# Revit family: BMP250710
name_source: partatom
category: Generic Models
revit_build: Autodesk Revit MEP 2014 (Build: 20130308_1515(x64)
units: mm (PartAtom-declared; Revit-internal decimal feet)

## types (2) — shared parameters
Depth = 538 mm  [stored 1.76509 ft]
Door Glass = Glass, Green
Height = 455 mm
Manufacturer = Gaggenau
URL = http://www.gaggenau.com.
Width = 590 mm  [stored 1.9357 ft]
oven = Metal Panel

## per-type parameters (varying)
| type | Description |
| BMP250710 | Gaggenau 200 series Combi-microwave oven, Gaggenau Metallic, right-hinged, controls at the top, flush design |
| BMP251710 | Gaggenau 200 series Combi-microwave oven, Gaggenau Metallic, left-hinged, controls at the top, flush design |

note: column(s) folded — value = type name in every type: Model

note: [stored X ft] marks values corroborated as IEEE doubles in the binary element streams (Revit-internal decimal feet)

## geometry (parser evidence)
native form markers: Blend x2, Sweep x3
no freeform markers — native parametric forms only
